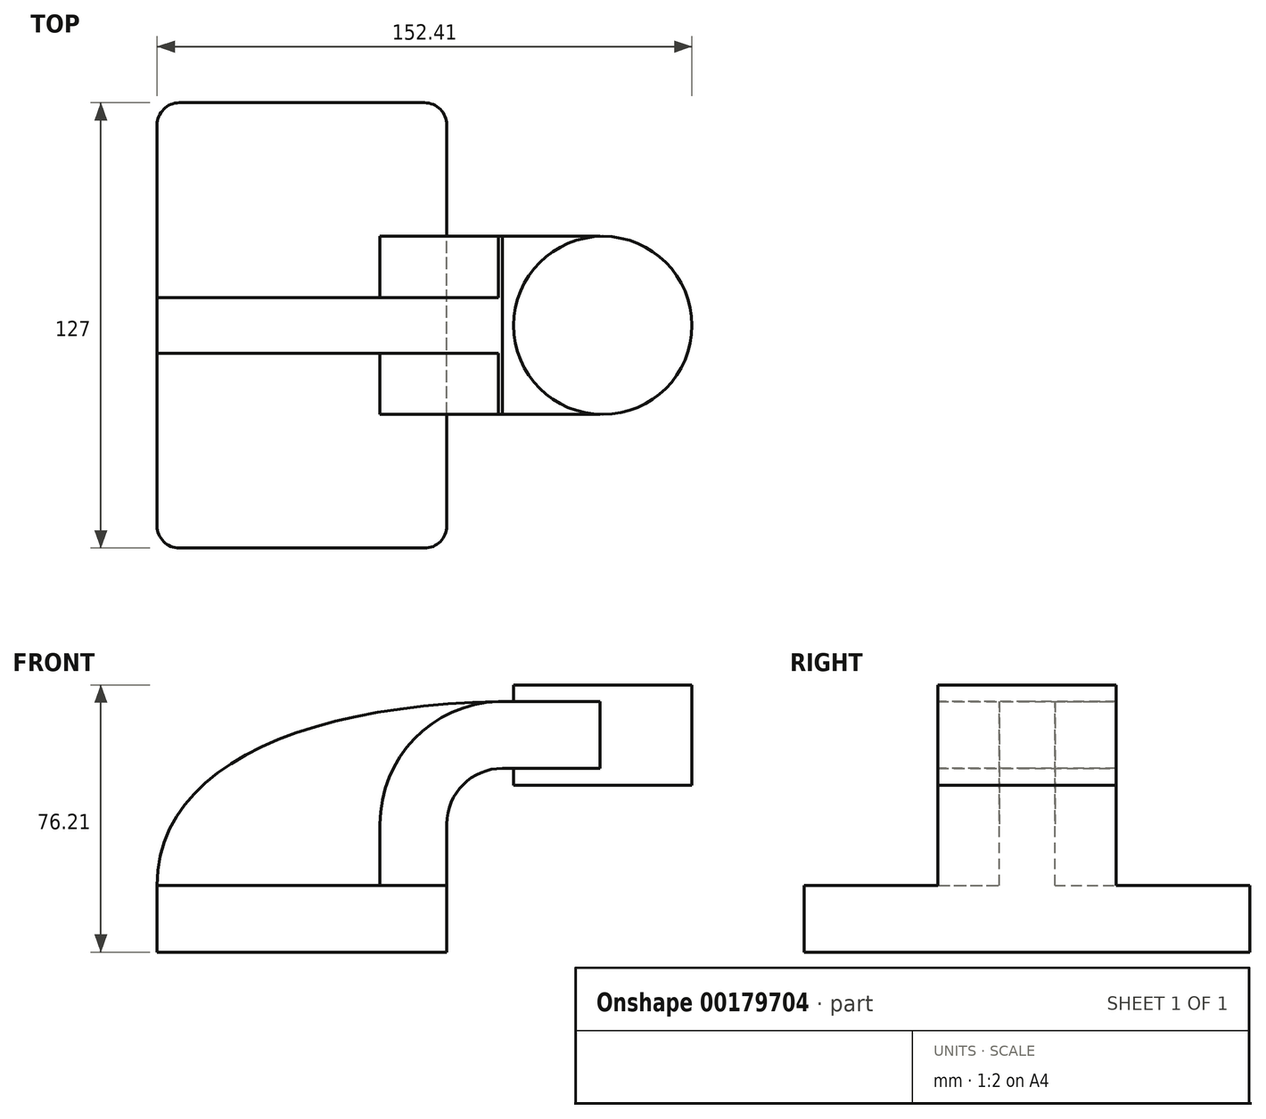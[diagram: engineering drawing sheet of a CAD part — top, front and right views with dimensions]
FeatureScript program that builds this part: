
annotation { "Feature Type Name" : "Feature", "Feature Type Description" : "" }
export const myFeature = defineFeature(function(context is Context, id is Id, definition is map)
    precondition{}
    {
        {
            var Q0;
            Q0=qCreatedBy(makeId("Front.planeOp"),FACE);
            var sketch = newSketch(context, id + "F0", { "sketchPlane" : qUnion([Q0])});
            skLineSegment(sketch, "E0.bottom", {"start": v(41.27, 9.53) * mm, "end": v(-41.28, 9.53) * mm});
            skLineSegment(sketch, "E0.top", {"start": v(41.28, -9.52) * mm, "end": v(-41.27, -9.52) * mm});
            skLineSegment(sketch, "E0.left", {"start": v(41.27, 9.53) * mm, "end": v(41.28, -9.52) * mm});
            skLineSegment(sketch, "E0.right", {"start": v(-41.28, 9.53) * mm, "end": v(-41.27, -9.52) * mm});
            skPoint(sketch, "E0.middle", {"position": v(0, 0) * mm});
            skLineSegment(sketch, "E1.bottom", {"start": v(111.12, 38.1) * mm, "end": v(60.32, 38.1) * mm});
            skLineSegment(sketch, "E1.top", {"start": v(111.12, 66.68) * mm, "end": v(60.32, 66.68) * mm});
            skLineSegment(sketch, "E1.left", {"start": v(111.12, 38.1) * mm, "end": v(111.12, 66.68) * mm});
            skLineSegment(sketch, "E1.right", {"start": v(60.32, 38.1) * mm, "end": v(60.32, 66.68) * mm});
            skPoint(sketch, "E1.middle", {"position": v(85.72, 52.39) * mm});
            skLineSegment(sketch, "E2", {"start": v(41.27, 9.53) * mm, "end": v(41.27, 27) * mm});
            skArc(sketch, "E3", {"start": v(41.27, 27) * mm, "mid": v(45.92, 38.23) * mm, "end": v(57.15, 42.88) * mm});
            skLineSegment(sketch, "E4", {"start": v(57.15, 42.88) * mm, "end": v(84.9, 42.88) * mm});
            skLineSegment(sketch, "E5.0", {"start": v(57.15, 61.93) * mm, "end": v(84.9, 61.93) * mm});
            skArc(sketch, "E5.1", {"start": v(22.22, 27) * mm, "mid": v(32.45, 51.7) * mm, "end": v(57.15, 61.93) * mm});
            skLineSegment(sketch, "E5.2", {"start": v(22.22, 9.53) * mm, "end": v(22.22, 27) * mm});
            skLineSegment(sketch, "E6", {"start": v(84.9, 42.88) * mm, "end": v(84.9, 61.93) * mm});
            skFitSpline(sketch, "E7", {"points": [v(-41.28, 9.53) * mm, v(57.15, 61.93) * mm], "startDerivative": vector(0.06, 101.02) * mm, "endDerivative": vector(171.45, 2.63) * mm});
            skLineSegment(sketch, "E8", {"start": v(85.72, 38.1) * mm, "end": v(85.72, 66.68) * mm});
            skSolve(sketch);
        }
        {
            var Q0;
            Q0=makeQuery(id+"F0.imprint","IMPRINT",FACE,{"disambiguationData":[TD([[makeQuery(id+"F0.imprint","IMPRINT",EDGE,{"derivedFrom":sQuery(id+"F0.wireOp",EDGE,"E0.top")}),-1.0]])]});
            extrude(context, id + "F1", {"entities" : qUnion([Q0]), "endBound" : BoundingType.SYMMETRIC, "depth" : 127 * mm});
        }
        {
            var Q0;
            {var subQ1=sQuery(id+"F0.wireOp",EDGE,"E2");Q0=makeQuery(id+"F0.imprint","IMPRINT",FACE,{"disambiguationData":[TD([[makeQuery(id+"F0.imprint","IMPRINT",EDGE,{"derivedFrom":subQ1}),1.0]])]});}
            var Q1;
            {var subQ5=sQuery(id+"F0.wireOp",EDGE,"E6");Q1=makeQuery(id+"F0.imprint","IMPRINT",FACE,{"disambiguationData":[TD([[makeQuery(id+"F0.imprint","IMPRINT",EDGE,{"derivedFrom":subQ5}),1.0]])]});}
            extrude(context, id + "F2", {"entities" : qUnion([Q0, Q1]), "operationType" : NewBodyOperationType.ADD, "endBound" : BoundingType.SYMMETRIC, "depth" : 50.8 * mm});
        }
        {
            var Q0;
            {var subQ3=sQuery(id+"F0.wireOp",EDGE,"E5.2");Q0=makeQuery(id+"F0.imprint","IMPRINT",FACE,{"disambiguationData":[TD([[makeQuery(id+"F0.imprint","IMPRINT",EDGE,{"derivedFrom":subQ3}),1.0]])]});}
            extrude(context, id + "F3", {"entities" : qUnion([Q0]), "operationType" : NewBodyOperationType.ADD, "endBound" : BoundingType.SYMMETRIC, "depth" : 15.88 * mm});
        }
        {
            var Q0;
            {var subQ0=sQuery(id+"F0.wireOp",EDGE,"E1.left");Q0=makeQuery(id+"F0.imprint","IMPRINT",FACE,{"disambiguationData":[TD([[makeQuery(id+"F0.imprint","IMPRINT",EDGE,{"derivedFrom":subQ0}),1.0]])]});}
            var Q1;
            Q1=sQuery(id+"F0.wireOp",EDGE,"E8");
            revolve(context, id + "F4", {"operationType" : NewBodyOperationType.ADD, "entities" : qUnion([Q0]), "axis" : qUnion([Q1]), "revolveType" : RevolveType.FULL});
        }
        {
            var Q0;
            Q0=makeQuery(id+"F1.opExtrude","CAP_EDGE",EDGE,{"disambiguationData":[OSD([sQuery(id+"F0.wireOp",EDGE,"E0.right")])],"isStart":false});
            var Q1;
            Q1=makeQuery(id+"F1.opExtrude","CAP_EDGE",EDGE,{"disambiguationData":[OSD([sQuery(id+"F0.wireOp",EDGE,"E0.left")])],"isStart":false});
            var Q2;
            Q2=makeQuery(id+"F1.opExtrude","CAP_EDGE",EDGE,{"disambiguationData":[OSD([sQuery(id+"F0.wireOp",EDGE,"E0.left")])],"isStart":true});
            var Q3;
            Q3=makeQuery(id+"F1.opExtrude","CAP_EDGE",EDGE,{"disambiguationData":[OSD([sQuery(id+"F0.wireOp",EDGE,"E0.right")])],"isStart":true});
            fillet(context, id + "F5", {"entities" : qUnion([Q0, Q1, Q2, Q3]), "radius" : 6.35 * mm, "tangentPropagation" : true, "allowEdgeOverflow" : false});
        }
    });
